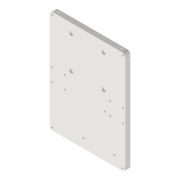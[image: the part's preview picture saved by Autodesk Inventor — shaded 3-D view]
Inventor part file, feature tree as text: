
AUTODESK INVENTOR PART (.ipt)
format: ipt  version: 2022 (Build 260153000, 153)  size: 190,976 bytes
history: native  units: mm
features: sketch x9, reference x9, extrude x5, projected_geometry x5, other x4, hole x3, plane x2
ambient origin geometry x8: Origin, YZ Plane, XZ Plane, XY Plane, X Axis, Y Axis, Z Axis, Center Point
bodies: Volumenkörper1 (feature_tree)
feature tree (37):
  plane  "Arbeitsebene1"
  sketch  "Skizze1"  dims[d1=0.0mm d13=20.0mm]
  plane  "Arbeitsebene2"
  extrude  "Extrusion1"  Depth=20.0mm
  hole  "Bohrung1"  [1 undecoded]
  hole  "Bohrung2"  [1 undecoded]
  extrude  "Extrusion3"  Depth=5.0mm
  extrude  "Extrusion4"  Depth=10.0mm TaperAngle=0.0deg
  extrude  "Extrusion5"  Depth=2.8mm
  extrude  "Extrusion6"  Depth=5.0mm
  hole  "Bohrung3"  [1 undecoded]
  sketch  "Skizze2"  dims[d14=20.0mm d15=20.0mm]
  reference  "Referenz1"
  reference  "Referenz2"
  reference  "Referenz3"
  reference  "Referenz4"
  reference  "Referenz5"
  sketch  "Skizze4"  dims[d16=20.0mm]
  projected_geometry  "Projizierte Kontur2"
  sketch  "Skizze5"  dims[d21=2.8mm d22=6.0mm d23=7.0mm d24=10.0mm d25=90.0deg d26=8.0mm d27=20.594885mm]
  reference  "Referenz6"
  sketch  "Skizze6"  dims[d28=2.8mm d29=6.0mm d30=6.5mm d31=3.0mm d32=90.0deg d33=8.0mm d34=20.594885mm d52=2.8mm]
  projected_geometry  "Projizierte Kontur3"
  sketch  "Skizze7"  dims[d53=2.8mm d54=5.0mm]
  projected_geometry  "Projizierte Kontur4"
  sketch  "Skizze8"  dims[d55=5.0mm d56=10.0mm d57=0.0mm]
  projected_geometry  "Projizierte Kontur5"
  sketch  "Skizze9"  dims[d58=2.8mm d59=2.8mm]
  projected_geometry  "Projizierte Kontur6"
  sketch  "Skizze10"  dims[d60=5.0mm d61=5.0mm d62=10.0mm d63=0.0mm d64=10.0mm d65=0.0mm d66=10.0mm d67=0.0mm d68=4.0mm d69=0.0mm d70=4.0mm d71=4.0mm d72=2.8mm d73=6.0mm d74=6.5mm d75=4.0mm d76=90.0deg d77=8.0mm d78=20.594885mm]
  reference  "Referenz9"
  reference  "Referenz10"
  reference  "Referenz11"
  other  "Omnicscope_Xiao.iam"
  other  "Omniscope_USBC_Wellplatemount2:1"
  other  "00_linear_z_stage_60mm:1"
  other  "00_Arduino_CNC_Assembly:1"
note: 3 required parameter values undecoded (feature->parameter linkage not recoverable at this tier; creation-order binding heuristic only, values carry confidence <= 0.55)
